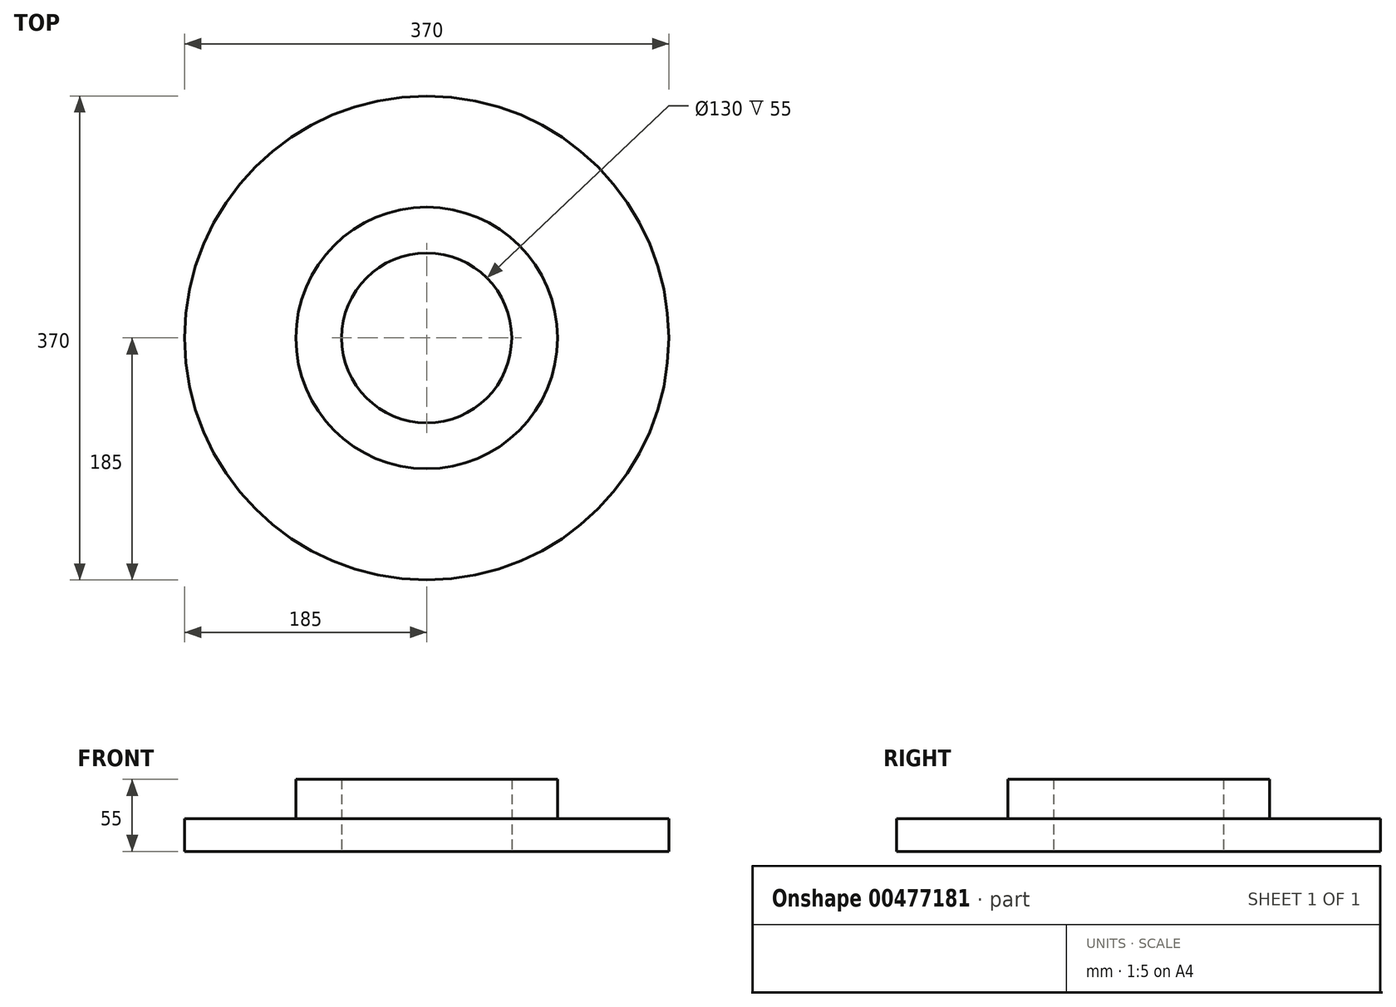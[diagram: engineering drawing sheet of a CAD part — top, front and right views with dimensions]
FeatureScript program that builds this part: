
annotation { "Feature Type Name" : "Feature", "Feature Type Description" : "" }
export const myFeature = defineFeature(function(context is Context, id is Id, definition is map)
    precondition{}
    {
        {
            var Q0;
            Q0=qCreatedBy(makeId("Top.planeOp"),FACE);
            var sketch = newSketch(context, id + "F0", { "sketchPlane" : qUnion([Q0])});
            skCircle(sketch, "E0", {"center": v(0, 0) * mm, "radius": 185 * mm});
            skSolve(sketch);
        }
        {
            var Q0;
            Q0=qSketchRegion(id+"F0",true);
            extrude(context, id + "F1", {"entities" : qUnion([Q0]), "depth" : 25 * mm});
        }
        {
            var Q0;
            Q0=makeQuery(id+"F1.opExtrude","CAP_FACE",FACE,{"disambiguationData":[OSD([sQuery(id+"F0.wireOp",EDGE,"E0")])],"isStart":false});
            var sketch = newSketch(context, id + "F2", { "sketchPlane" : qUnion([Q0])});
            skCircle(sketch, "E1", {"center": v(0, 0) * mm, "radius": 65 * mm});
            skCircle(sketch, "E2", {"center": v(0, 0) * mm, "radius": 100 * mm});
            skSolve(sketch);
        }
        {
            var Q0;
            Q0 = qSketchRegion(id + "F2", true);
            extrude(context, id + "F3", {"entities" : qUnion([Q0]), "operationType" : NewBodyOperationType.ADD, "depth" : 30 * mm});
        }
        {
            var Q0;
            Q0=makeQuery(id+"F3.boolean.opBoolean","SPLIT",FACE,{"disambiguationData":[TD([makeQuery(id+"F3.opExtrude","SWEPT_FACE",FACE,{"disambiguationData":[OSD([sQuery(id+"F2.wireOp",EDGE,"E1")])]})])],"derivedFrom":makeQuery(id+"F1.opExtrude","CAP_FACE",FACE,{"disambiguationData":[OSD([sQuery(id+"F0.wireOp",EDGE,"E0")])],"isStart":false})});
            extrude(context, id + "F4", {"entities" : qUnion([Q0]), "operationType" : NewBodyOperationType.REMOVE, "endBound" : BoundingType.THROUGH_ALL, "oppositeDirection" : true, "depth" : 25 * mm});
        }
    });
